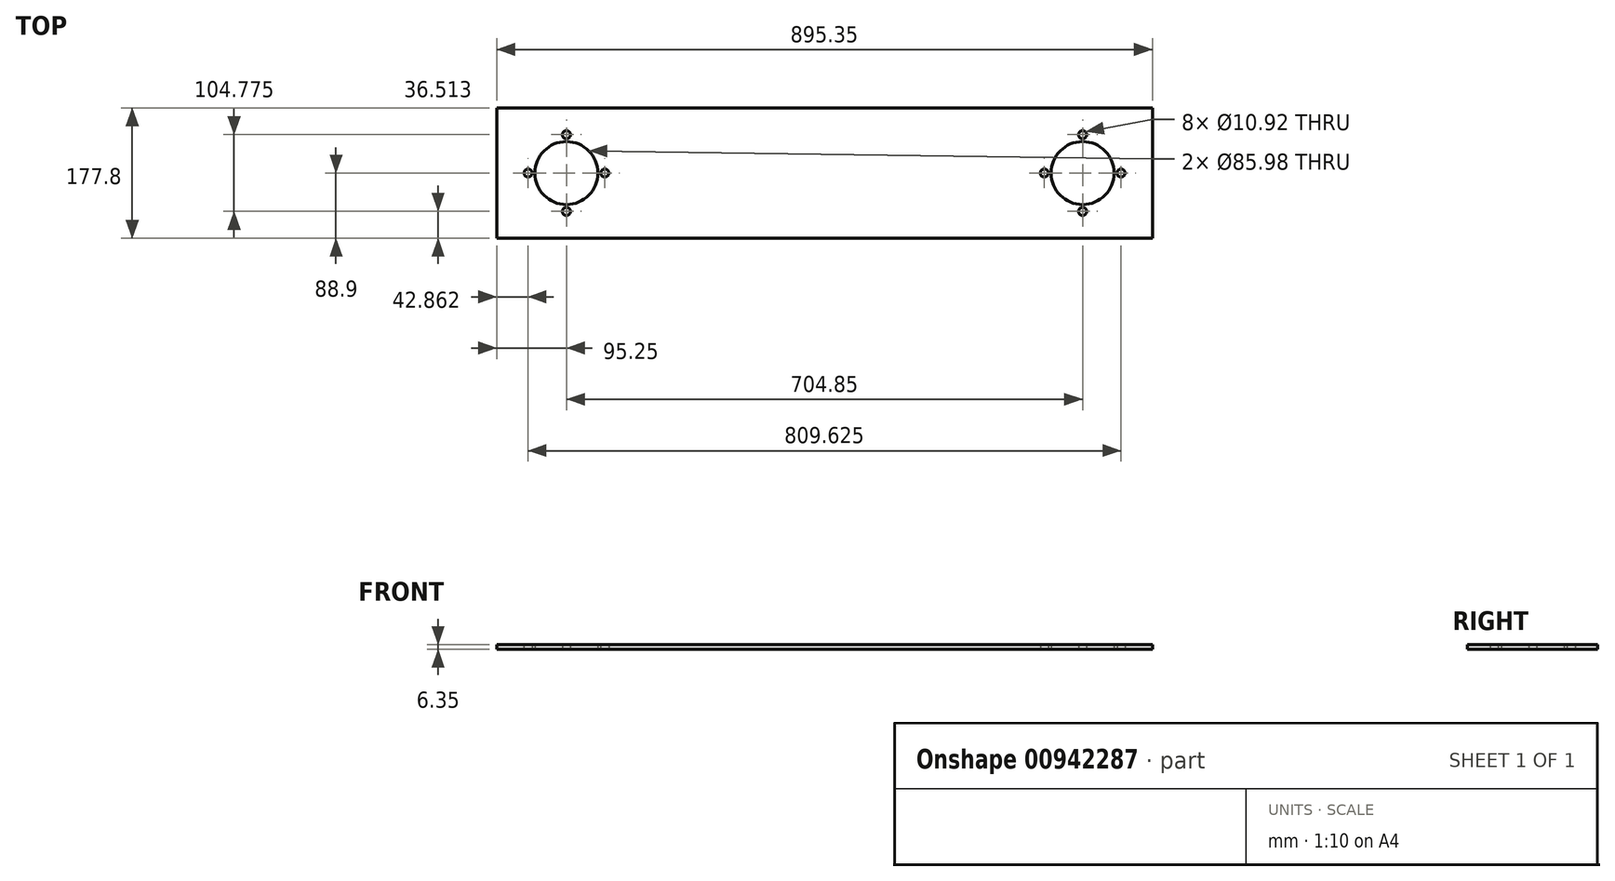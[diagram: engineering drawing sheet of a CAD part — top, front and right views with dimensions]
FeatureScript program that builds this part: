
annotation { "Feature Type Name" : "Feature", "Feature Type Description" : "" }
export const myFeature = defineFeature(function(context is Context, id is Id, definition is map)
    precondition{}
    {
        {
            var Q0;
            Q0=qCreatedBy(makeId("Top.planeOp"),FACE);
            var sketch = newSketch(context, id + "F0", { "sketchPlane" : qUnion([Q0])});
            skCircle(sketch, "E0", {"center": v(0, 0) * mm, "radius": 42.99 * mm});
            skCircle(sketch, "E1", {"center": v(0, 52.39) * mm, "radius": 5.46 * mm});
            skCircle(sketch, "E2.1.0", {"center": v(-52.39, 0) * mm, "radius": 5.46 * mm});
            skCircle(sketch, "E2.2.0", {"center": v(0, -52.39) * mm, "radius": 5.46 * mm});
            skCircle(sketch, "E2.3.0", {"center": v(52.39, 0) * mm, "radius": 5.46 * mm});
            skLineSegment(sketch, "E3.bottom", {"start": v(-95.25, -88.9) * mm, "end": v(800.1, -88.9) * mm});
            skLineSegment(sketch, "E3.top", {"start": v(-95.25, 88.9) * mm, "end": v(800.1, 88.9) * mm});
            skLineSegment(sketch, "E3.left", {"start": v(-95.25, -88.9) * mm, "end": v(-95.25, 88.9) * mm});
            skLineSegment(sketch, "E3.right", {"start": v(800.1, -88.9) * mm, "end": v(800.1, 88.9) * mm});
            skLineSegment(sketch, "E4", {"start": v(352.43, 88.9) * mm, "end": v(352.43, -24.46) * mm});
            skCircle(sketch, "E5.MirrorC", {"center": v(652.46, 0) * mm, "radius": 5.46 * mm});
            skCircle(sketch, "E6.MirrorC", {"center": v(704.85, 0) * mm, "radius": 42.99 * mm});
            skCircle(sketch, "E7.MirrorC", {"center": v(704.85, -52.39) * mm, "radius": 5.46 * mm});
            skCircle(sketch, "E8.MirrorC", {"center": v(757.24, 0) * mm, "radius": 5.46 * mm});
            skCircle(sketch, "E9.MirrorC", {"center": v(704.85, 52.39) * mm, "radius": 5.46 * mm});
            skSolve(sketch);
        }
        {
            var Q0;
            Q0=makeQuery(id+"F0.imprint","IMPRINT",FACE,{"disambiguationData":[TD([[makeQuery(id+"F0.imprint","IMPRINT",EDGE,{"derivedFrom":sQuery(id+"F0.wireOp",EDGE,"E0")}),-1.0]])]});
            extrude(context, id + "F1", {"entities" : qUnion([Q0]), "depth" : 6.35 * mm, "offsetDistance" : 25.4 * mm});
        }
    });
